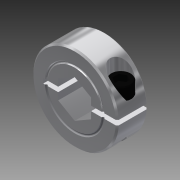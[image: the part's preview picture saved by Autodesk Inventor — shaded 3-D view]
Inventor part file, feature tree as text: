
AUTODESK INVENTOR PART (.ipt)
format: ipt  version: 2016 SP1 (Build 200210100, 210)  size: 260,608 bytes
history: native  units: in
note: dims shown in document units (in); Inventor stores cm internally (conversion verified against a paired STEP export)
features: extrude x2, sketch x2, other x1, imported_body x1
ambient origin geometry x8: Origin, YZ Plane, XZ Plane, XY Plane, X Axis, Y Axis, Z Axis, Center Point
bodies: Solid1 (feature_tree)
feature tree (6):
  other  "CL-8-A1"
  extrude  "Extrusion1"  Depth=0.4375in TaperAngle=0.0deg
  extrude  "Extrusion2"  [1 undecoded]
  imported_body  "Base1"
  sketch  "Sketch2"  dims[d0=0.5in d1=0.4375in d2=0.0in]
  sketch  "Sketch3"  dims[d3=1.0in d4=0.0in]
note: 1 required parameter value undecoded (feature->parameter linkage not recoverable at this tier; creation-order binding heuristic only, values carry confidence <= 0.55)
